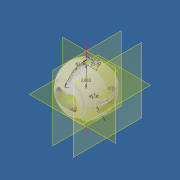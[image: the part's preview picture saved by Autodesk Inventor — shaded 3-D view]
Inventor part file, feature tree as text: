
AUTODESK INVENTOR PART (.ipt)
format: ipt  version: 2018.3 (Build 223284000, 284)  size: 1,072,128 bytes
history: native  units: in
note: dims shown in document units (in); Inventor stores cm internally (conversion verified against a paired STEP export)
features: sketch x17, revolve x8, chamfer x8, mirror x7, plane x6, fillet x5, projected_geometry x4, other x3, extrude x2
ambient origin geometry x8: Origin, YZ Plane, XZ Plane, XY Plane, X Axis, Y Axis, Z Axis, Center Point
bodies: Solid1 (feature_tree)
feature tree (60):
  other  "Wheatly.ipt"
  sketch  "Sketch2"  dims[d0=0.3937in d1=2.5in]
  sketch  "Sketch3"  dims[d2=6.0in d3=0.3966in]
  plane  "Work Plane1"
  revolve  "Revolution1"  [1 undecoded]
  mirror  "Mirror1"
  plane  "Work Plane2"
  extrude  "Extrusion1"  Depth=0.3966in
  sketch  "Sketch6"  dims[d11=2.8in d12=1.0in d13=0.0in]
  revolve  "Revolution2"  [1 undecoded]
  fillet  "Fillet1"  Radius=0.375in
  fillet  "Fillet2"  Radius=0.25in
  fillet  "Fillet3"  Radius=3.1in
  fillet  "Fillet4"  Radius=0.4438in
  chamfer  "Chamfer1"  Distance=1.0in
  chamfer  "Chamfer2"  Distance=0.13in
  chamfer  "Chamfer3"  Distance=0.13in
  chamfer  "Chamfer4"  Distance=0.13in
  chamfer  "Chamfer5"  Distance=0.13in
  chamfer  "Chamfer6"  Distance=0.13in
  chamfer  "Chamfer7"  Distance=0.13in
  chamfer  "Chamfer8"  Distance=0.13in
  sketch  "Sketch8"  dims[d15=5.7in]
  sketch  "Sketch9"  dims[d16=0.5in]
  plane  "Work Plane3"
  mirror  "Mirror2"
  plane  "Work Plane4"
  revolve  "Revolution3"  [1 undecoded]
  plane  "Work Plane5"
  mirror  "Mirror3"
  revolve  "Revolution4"  Angle=45.0deg
  sketch  "Sketch16"  dims[d19=0.1in]
  revolve  "Revolution5"  [1 undecoded]
  revolve  "Revolution6"  [1 undecoded]
  mirror  "Mirror4"
  sketch  "Sketch20"  dims[d22=0.1in]
  revolve  "Revolution8"  [1 undecoded]
  mirror  "Mirror5"
  revolve  "Revolution9"  [1 undecoded]
  plane  "Work Plane6"
  extrude  "Extrusion2"  Depth=2.75in
  fillet  "Fillet5"  Radius=6.1in
  mirror  "Mirror6"
  mirror  "Mirror7"
  other  "Solid1::Wheatly.ipt"
  other  "TaggingFeature1"
  sketch  "Sketch4"  dims[d4=0.3966in d5=0.75in d6=0.375in d7=0.25in d8=3.1in d9=0.4438in]
  sketch  "Sketch5"  dims[d10=-3.0in]
  sketch  "Sketch7"  dims[d14=0.4192in]
  sketch  "Sketch10"  dims[d17=0.25in]
  projected_geometry  "Projected Loop1"
  projected_geometry  "Projected Loop2"
  projected_geometry  "Projected Loop3"
  sketch  "Sketch15"  dims[d18=0.15in]
  sketch  "Sketch17"  dims[d20=0.1in]
  sketch  "Sketch18"  dims[d21=0.15in]
  sketch  "Sketch21"  dims[d23=2.0752in]
  projected_geometry  "Projected Loop4"
  sketch  "Sketch22"  dims[d24=0.075in]
  sketch  "Sketch23"  dims[d25=0.025in d26=0.13in d27=0.1in d28=1.2025in d29=0.13in d30=0.1in d31=1.2025in d32=0.13in d33=0.1in d34=1.2025in d35=0.13in d36=0.1in d37=1.2025in d38=0.13in d39=0.1in d40=1.2025in d41=0.13in d42=0.1in d43=1.2025in d44=0.13in d45=0.1in d46=1.2025in d47=0.13in d48=0.1in d49=1.2025in d50=45.0deg d51=3.0in d52=2.0752in d53=2.875in d55=1.5in d62=2.85in d63=2.85in d64=6.1in d65=6.0in d66=60.0deg d67=2.0in d69=60.0deg d71=1.5in d72=60.0deg d75=2.8031in d76=0.1747in d77=6.0in d78=0.327in d79=0.327in d80=0.6871in d81=0.3172in d82=0.3172in d83=0.15in d84=3.0in d85=0.2in d88=0.075in d89=0.6871in d90=1.8in d91=2.75in d92=3.1in d93=0.8in d94=0.0in]
note: 7 required parameter values undecoded (feature->parameter linkage not recoverable at this tier; creation-order binding heuristic only, values carry confidence <= 0.55)
